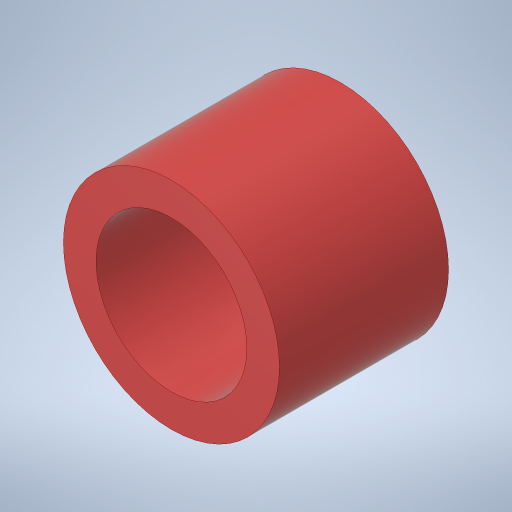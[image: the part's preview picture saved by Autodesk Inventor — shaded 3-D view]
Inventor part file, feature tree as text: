
AUTODESK INVENTOR PART (.ipt)
format: ipt  version: 2023.4 (Build 274418000, 418)  size: 251,392 bytes
history: native  units: in
note: dims shown in document units (in); Inventor stores cm internally (conversion verified against a paired STEP export)
features: extrude x1
ambient origin geometry x8: Origin, YZ Plane, XZ Plane, XY Plane, X Axis, Y Axis, Z Axis, Center Point
bodies: Solid1 (feature_tree)
feature tree (1):
  extrude  "Extrusion1"  TaperAngle=0.0deg  [1 undecoded]
note: 1 required parameter value undecoded (feature->parameter linkage not recoverable at this tier; creation-order binding heuristic only, values carry confidence <= 0.55)
